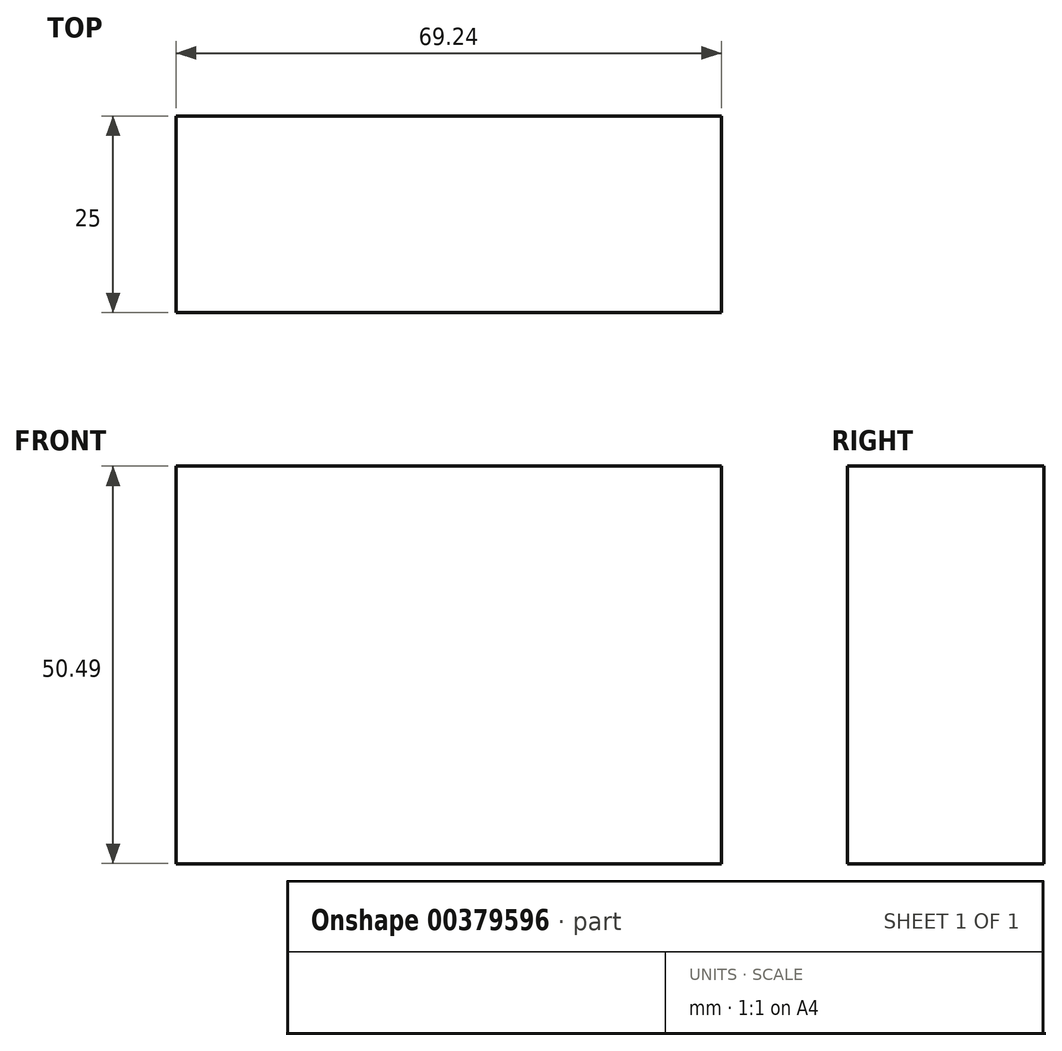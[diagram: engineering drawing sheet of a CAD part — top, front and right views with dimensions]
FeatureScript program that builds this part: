
annotation { "Feature Type Name" : "Feature", "Feature Type Description" : "" }
export const myFeature = defineFeature(function(context is Context, id is Id, definition is map)
    precondition{}
    {
        {
            var Q0;
            Q0=qCreatedBy(makeId("Front.planeOp"),FACE);
            var sketch = newSketch(context, id + "F0", { "sketchPlane" : qUnion([Q0])});
            skLineSegment(sketch, "E0.bottom", {"start": v(0, 0) * mm, "end": v(69.24, 0) * mm});
            skLineSegment(sketch, "E0.top", {"start": v(0, -50.5) * mm, "end": v(69.24, -50.5) * mm});
            skLineSegment(sketch, "E0.left", {"start": v(0, 0) * mm, "end": v(0, -50.5) * mm});
            skLineSegment(sketch, "E0.right", {"start": v(69.24, 0) * mm, "end": v(69.24, -50.5) * mm});
            skSolve(sketch);
        }
        {
            var Q0;
            Q0 = qSketchRegion(id + "F0", true);
            extrude(context, id + "F1", {"entities" : qUnion([Q0]), "depth" : 25 * mm});
        }
    });
